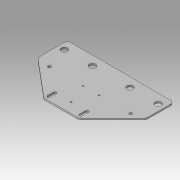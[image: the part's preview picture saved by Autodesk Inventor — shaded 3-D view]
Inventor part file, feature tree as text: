
AUTODESK INVENTOR PART (.ipt)
format: ipt  version: 2016 (Build 200138000, 138)  size: 216,064 bytes
history: native  units: in
note: dims shown in document units (in); Inventor stores cm internally (conversion verified against a paired STEP export)
features: sketch x7, extrude x4, hole x3
ambient origin geometry x8: Origin, YZ Plane, XZ Plane, XY Plane, X Axis, Y Axis, Z Axis, Center Point
bodies: Solid1 (feature_tree)
feature tree (14):
  extrude  "Extrusion1"  Depth=8.5in
  hole  "Hole1"  [1 undecoded]
  extrude  "Extrusion3"  Depth=3.1102in
  extrude  "Extrusion4"  Depth=0.25in
  extrude  "Extrusion5"  Depth=1.0236in
  hole  "Hole3"  [1 undecoded]
  hole  "Hole2"  [1 undecoded]
  sketch  "Sketch1"  dims[d0=8.5in d1=6.0in]
  sketch  "Sketch2"  dims[d2=0.125in d3=0.0in d4=5.6831in]
  sketch  "Sketch3"  dims[d5=1.0236in d7=3.1102in]
  sketch  "Sketch5"  dims[d12=0.2362in d13=0.75in d14=0.375in d15=0.25in d16=0.5635in d17=1.0in d18=0.8108in d19=1.0768in]
  sketch  "Sketch7"  dims[d20=3.1102in d21=1.0236in]
  sketch  "Sketch8"  dims[d22=3.124in d23=7.5728in]
  sketch  "Sketch10"  dims[d24=0.2953in d40=3.8881in d43=1.0in d44=0.0in d45=1.75in d47=1.75in d48=1.75in d49=1.75in d50=2.382in d52=2.5591in d53=0.6398in d54=0.6398in d55=2.382in d58=2.0472in d62=1.2795in d64=0.1181in d65=0.75in d66=0.375in d67=0.25in d68=0.5635in d69=1.0in d70=0.8108in d72=0.2362in d76=0.236in d77=0.492in d78=0.236in d79=0.492in d80=1.0in d81=0.0in d82=0.236in d83=0.492in d84=0.236in d85=0.492in d86=1.0in d87=0.0in d88=0.2362in d93=0.2953in d96=2.07in d99=135.0deg d100=0.25in d101=0.25in d102=0.25in d103=0.25in d104=0.962in d110=0.5in d111=2.25in d112=3.0in d113=2.25in d116=0.0007in d117=0.75in d118=0.5in d119=0.75in d120=0.375in d121=0.25in d122=0.5635in d123=1.0in d124=0.8108in d125=0.0in d126=2.5165in d127=0.3731in d128=2.0866in]
note: 3 required parameter values undecoded (feature->parameter linkage not recoverable at this tier; creation-order binding heuristic only, values carry confidence <= 0.55)
